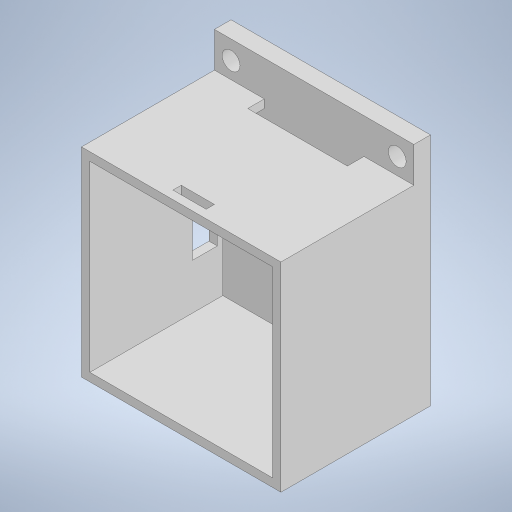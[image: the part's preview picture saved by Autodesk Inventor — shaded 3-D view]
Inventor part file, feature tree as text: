
AUTODESK INVENTOR PART (.ipt)
format: ipt  version: 2023 (Build 270158000, 158)  size: 270,848 bytes
history: native  units: in
note: dims shown in document units (in); Inventor stores cm internally (conversion verified against a paired STEP export)
features: extrude x5, sketch x5, projected_geometry x4
ambient origin geometry x8: Origin, YZ Plane, XZ Plane, XY Plane, X Axis, Y Axis, Z Axis, Center Point
bodies: Solid1 (feature_tree)
feature tree (14):
  extrude  "Extrusion1"  Depth=3.0in
  extrude  "Extrusion2"  Depth=1.5in
  extrude  "Extrusion4"  Depth=0.125in
  extrude  "Extrusion5"  Depth=0.125in
  extrude  "Extrusion6"  Depth=2.0in TaperAngle=0.0deg
  sketch  "Sketch1"  dims[d0=3.0in d1=3.0in]
  sketch  "Sketch2"  dims[d2=1.5in d3=1.5in]
  sketch  "Sketch4"  dims[d4=0.25in d5=0.0in d6=0.125in]
  projected_geometry  "Projected Loop1"
  sketch  "Sketch5"  dims[d7=0.125in d8=0.125in]
  projected_geometry  "Projected Loop2"
  sketch  "Sketch6"  dims[d9=0.125in d10=2.0in d11=0.0in d14=0.5625in d15=0.375in d16=0.25in d17=0.0in d18=0.27in d19=0.27in d20=2.5in d22=0.2812in d23=0.2812in d24=0.25in d25=0.0in d26=1.5in d27=3.0in d28=1.5in d29=0.25in d30=0.5625in d31=0.0in d32=0.5in d33=0.125in d34=0.25in d35=0.125in d36=0.25in d37=3.0in d38=1.25in]
  projected_geometry  "Projected Loop3"
  projected_geometry  "Projected Loop4"
